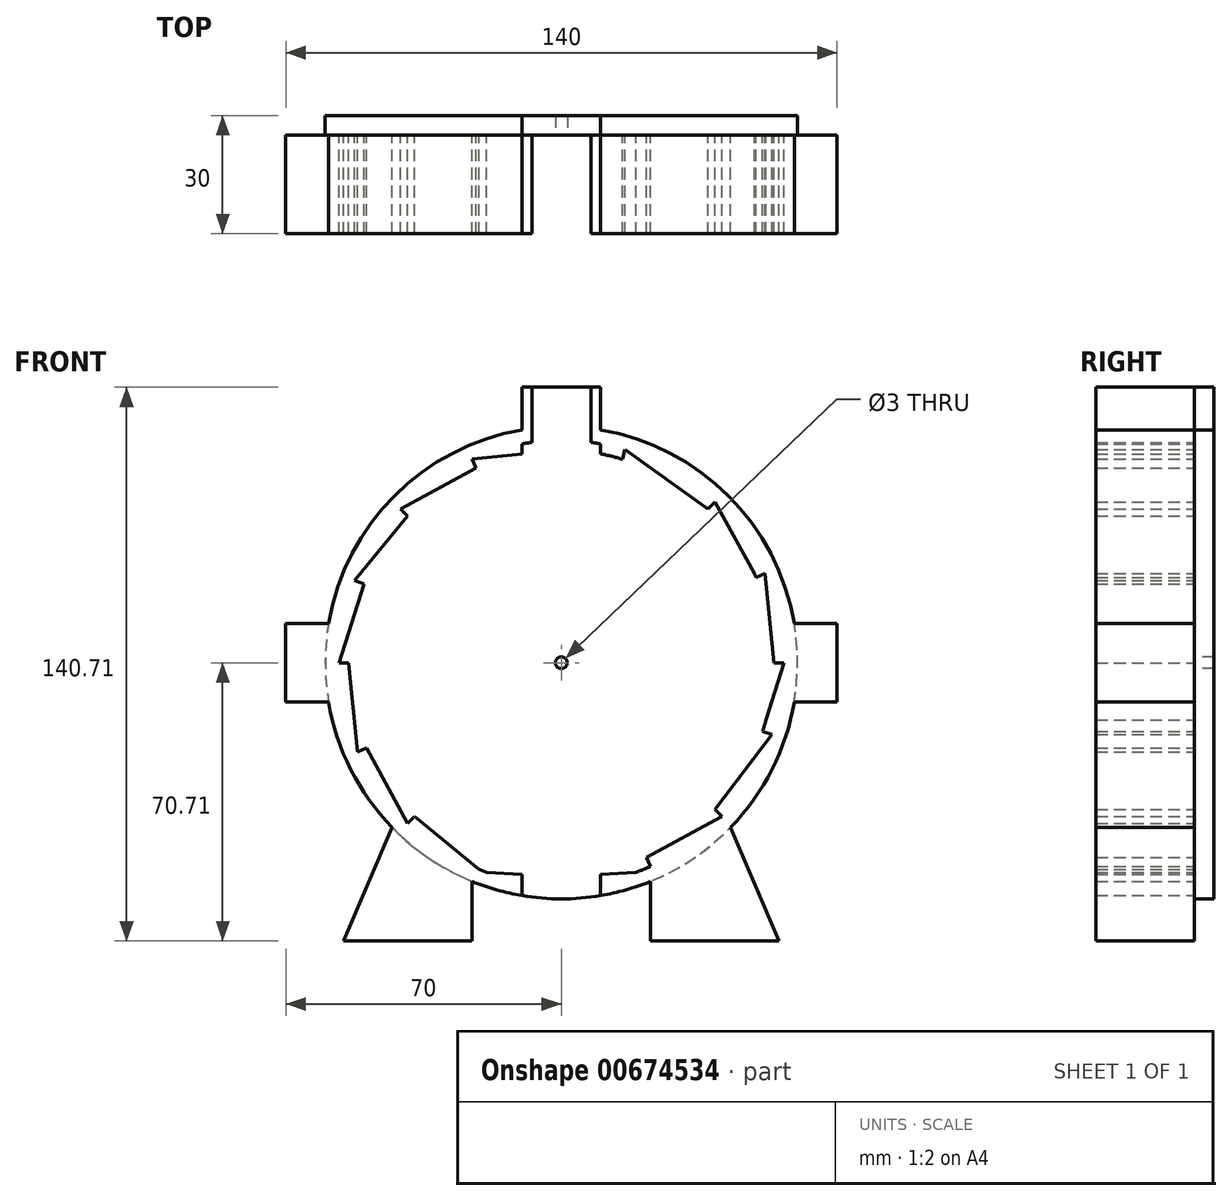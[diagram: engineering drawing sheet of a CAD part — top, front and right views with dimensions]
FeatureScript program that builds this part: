
annotation { "Feature Type Name" : "Feature", "Feature Type Description" : "" }
export const myFeature = defineFeature(function(context is Context, id is Id, definition is map)
    precondition{}
    {
        {
            var Q0;
            Q0=qCreatedBy(makeId("Front.planeOp"),FACE);
            var sketch = newSketch(context, id + "F0", { "sketchPlane" : qUnion([Q0])});
            skArc(sketch, "E0", {"start": v(-20.88, -52.5) * mm, "mid": v(-19.94, -52.87) * mm, "end": v(-18.99, -53.21) * mm});
            skArc(sketch, "E1", {"start": v(-22.63, -55.57) * mm, "mid": v(-16.42, -57.71) * mm, "end": v(-10, -59.16) * mm});
            skLineSegment(sketch, "E2", {"start": v(-10, 70) * mm, "end": v(-7.5, 70) * mm});
            skLineSegment(sketch, "E3", {"start": v(-7.5, 56) * mm, "end": v(-7.5, 70) * mm});
            skPoint(sketch, "E4.orphan", {"position": v(10, -70) * mm});
            skPoint(sketch, "E5.trimOffspring.end.orphan", {"position": v(-10, -70) * mm});
            skPoint(sketch, "E6.end.orphan", {"position": v(-17.52, -53.71) * mm});
            skPoint(sketch, "E7.orphan", {"position": v(10, -53.71) * mm});
            skPoint(sketch, "E8.MirrorCS.end.orphan", {"position": v(17.52, -53.71) * mm});
            skLineSegment(sketch, "E9", {"start": v(10, -53.71) * mm, "end": v(18.99, -53.21) * mm});
            skLineSegment(sketch, "E10.MirrorCS", {"start": v(-10, -53.71) * mm, "end": v(-18.99, -53.21) * mm});
            skLineSegment(sketch, "E11", {"start": v(56.5, 0) * mm, "end": v(54, 0) * mm});
            skLineSegment(sketch, "E12", {"start": v(54, 0) * mm, "end": v(51.77, 22.63) * mm});
            skLineSegment(sketch, "E13", {"start": v(52.02, -14.5) * mm, "end": v(56.5, 0) * mm});
            skLineSegment(sketch, "E14", {"start": v(21.63, -49.48) * mm, "end": v(40.85, -39.04) * mm});
            skLineSegment(sketch, "E15", {"start": v(39.04, -37.3) * mm, "end": v(53.49, -18.2) * mm});
            skLineSegment(sketch, "E16", {"start": v(-37.3, -39.04) * mm, "end": v(-20.88, -52.5) * mm});
            skLineSegment(sketch, "E17", {"start": v(-49.48, -21.63) * mm, "end": v(-39.04, -40.85) * mm});
            skLineSegment(sketch, "E18", {"start": v(-54, 0) * mm, "end": v(-56.5, 0) * mm});
            skLineSegment(sketch, "E19", {"start": v(-54, 0) * mm, "end": v(-51.77, -22.63) * mm});
            skLineSegment(sketch, "E20", {"start": v(-50.18, 19.96) * mm, "end": v(-56.5, 0) * mm});
            skLineSegment(sketch, "E21", {"start": v(-39.04, 37.3) * mm, "end": v(-52.5, 20.88) * mm});
            skLineSegment(sketch, "E22", {"start": v(-21.63, 49.48) * mm, "end": v(-40.85, 39.04) * mm});
            skLineSegment(sketch, "E23", {"start": v(-10, 53.07) * mm, "end": v(-22.63, 51.77) * mm});
            skLineSegment(sketch, "E24", {"start": v(49.03, 22.63) * mm, "end": v(39.04, 40.85) * mm});
            skLineSegment(sketch, "E25", {"start": v(37.3, 39.04) * mm, "end": v(16.23, 54.12) * mm});
            skLineSegment(sketch, "E26", {"start": v(22.63, -55.57) * mm, "end": v(22.63, -70.7) * mm});
            skLineSegment(sketch, "E27", {"start": v(22.63, -70.7) * mm, "end": v(55.32, -70.7) * mm});
            skLineSegment(sketch, "E28", {"start": v(55.32, -70.7) * mm, "end": v(43.02, -41.82) * mm});
            skLineSegment(sketch, "E29.MirrorCS", {"start": v(-22.63, -55.57) * mm, "end": v(-22.63, -70.7) * mm});
            skLineSegment(sketch, "E30.MirrorCS", {"start": v(-55.32, -70.7) * mm, "end": v(-43.02, -41.82) * mm});
            skLineSegment(sketch, "E31.MirrorCS", {"start": v(-22.63, -70.7) * mm, "end": v(-55.32, -70.7) * mm});
            skLineSegment(sketch, "E32", {"start": v(-70, 0) * mm, "end": v(-70, -10) * mm});
            skLineSegment(sketch, "E33.MirrorCS", {"start": v(-70, 0) * mm, "end": v(-70, 10) * mm});
            skLineSegment(sketch, "E34.MirrorCS", {"start": v(70, 0) * mm, "end": v(70, 10) * mm});
            skLineSegment(sketch, "E35.MirrorCS", {"start": v(70, 0) * mm, "end": v(70, -10) * mm});
            skLineSegment(sketch, "E36", {"start": v(70, -10) * mm, "end": v(59.16, -10) * mm});
            skLineSegment(sketch, "E37", {"start": v(70, 10) * mm, "end": v(59.16, 10) * mm});
            skLineSegment(sketch, "E38.MirrorCS", {"start": v(-70, -10) * mm, "end": v(-59.16, -10) * mm});
            skLineSegment(sketch, "E39.MirrorCS", {"start": v(-70, 10) * mm, "end": v(-59.16, 10) * mm});
            skLineSegment(sketch, "E40.trimOffspring", {"start": v(-10, -53.71) * mm, "end": v(-10, -59.16) * mm});
            skPoint(sketch, "E41.orphan", {"position": v(-22.63, -51.77) * mm});
            skLineSegment(sketch, "E42.trimOffspring", {"start": v(-37.3, -39.04) * mm, "end": v(-39.04, -40.85) * mm});
            skLineSegment(sketch, "E43.trimOffspring", {"start": v(-49.48, -21.63) * mm, "end": v(-51.77, -22.63) * mm});
            skPoint(sketch, "E44.start.orphan", {"position": v(-60, 0) * mm});
            skArc(sketch, "E45.trimOffspring", {"start": v(-59.16, -10) * mm, "mid": v(-53.51, -27.14) * mm, "end": v(-43.02, -41.82) * mm});
            skArc(sketch, "E46.trimOffspring", {"start": v(18.99, -53.21) * mm, "mid": v(20.82, -52.52) * mm, "end": v(22.63, -51.77) * mm});
            skArc(sketch, "E47.trimOffspring", {"start": v(10, -59.16) * mm, "mid": v(16.42, -57.71) * mm, "end": v(22.63, -55.57) * mm});
            skLineSegment(sketch, "E48.trimOffspring", {"start": v(10, -53.71) * mm, "end": v(10, -59.16) * mm});
            skLineSegment(sketch, "E49.trimOffspring", {"start": v(21.63, -49.48) * mm, "end": v(22.63, -51.77) * mm});
            skArc(sketch, "E50.trimOffspring", {"start": v(43.02, -41.82) * mm, "mid": v(53.51, -27.14) * mm, "end": v(59.16, -10) * mm});
            skLineSegment(sketch, "E51.trimOffspring", {"start": v(39.04, -37.3) * mm, "end": v(40.85, -39.04) * mm});
            skArc(sketch, "E52.trimOffspring", {"start": v(51.12, -17.4) * mm, "mid": v(51.6, -15.95) * mm, "end": v(52.02, -14.5) * mm});
            skLineSegment(sketch, "E53.trimOffspring", {"start": v(51.12, -17.4) * mm, "end": v(53.49, -18.2) * mm});
            skArc(sketch, "E54.trimOffspring", {"start": v(49.48, 21.63) * mm, "mid": v(49.25, 22.13) * mm, "end": v(49.03, 22.63) * mm});
            skArc(sketch, "E55.trimOffspring", {"start": v(59.16, 10) * mm, "mid": v(42.43, 42.43) * mm, "end": v(10, 59.16) * mm});
            skPoint(sketch, "E56.MirrorCS.end.orphan", {"position": v(70, 0) * mm});
            skPoint(sketch, "E56.MirrorCS.start.orphan", {"position": v(60, 0) * mm});
            skLineSegment(sketch, "E57.trimOffspring", {"start": v(49.48, 21.63) * mm, "end": v(51.77, 22.63) * mm});
            skLineSegment(sketch, "E58.trimOffspring", {"start": v(-50.18, 19.96) * mm, "end": v(-52.5, 20.88) * mm});
            skLineSegment(sketch, "E59.trimOffspring", {"start": v(-39.04, 37.3) * mm, "end": v(-40.85, 39.04) * mm});
            skLineSegment(sketch, "E60.trimOffspring", {"start": v(-21.63, 49.48) * mm, "end": v(-22.63, 51.77) * mm});
            skLineSegment(sketch, "E61.trimOffspring", {"start": v(-10, 53.07) * mm, "end": v(-10, 55.6) * mm});
            skPoint(sketch, "E62.MirrorCS.end.orphan", {"position": v(-7.5, 46.44) * mm});
            skPoint(sketch, "E62.MirrorCS.start.orphan", {"position": v(-10, 46.44) * mm});
            skLineSegment(sketch, "E63.trimOffspring", {"start": v(-10, 59.16) * mm, "end": v(-10, 70) * mm});
            skArc(sketch, "E64.trimOffspring", {"start": v(-10, 59.16) * mm, "mid": v(-42.43, 42.43) * mm, "end": v(-59.16, 10) * mm});
            skArc(sketch, "E65.trimOffspring", {"start": v(-7.5, 56) * mm, "mid": v(-8.75, 55.82) * mm, "end": v(-10, 55.6) * mm});
            skLineSegment(sketch, "E66.trimOffspring", {"start": v(7.5, 70) * mm, "end": v(10, 70) * mm});
            skLineSegment(sketch, "E67.trimOffspring", {"start": v(7.5, 56) * mm, "end": v(7.5, 70) * mm});
            skPoint(sketch, "E68.end.orphan", {"position": v(7.5, 46.44) * mm});
            skPoint(sketch, "E68.start.orphan", {"position": v(10, 46.44) * mm});
            skLineSegment(sketch, "E69.trimOffspring", {"start": v(10, 53.07) * mm, "end": v(10, 55.6) * mm});
            skLineSegment(sketch, "E70.trimOffspring", {"start": v(15.51, 51.72) * mm, "end": v(16.23, 54.12) * mm});
            skArc(sketch, "E71.trimOffspring", {"start": v(15.51, 51.72) * mm, "mid": v(12.77, 52.47) * mm, "end": v(10, 53.07) * mm});
            skLineSegment(sketch, "E72.trimOffspring", {"start": v(37.3, 39.04) * mm, "end": v(39.04, 40.85) * mm});
            skArc(sketch, "E73.trimOffspring", {"start": v(10, 55.6) * mm, "mid": v(8.75, 55.82) * mm, "end": v(7.5, 56) * mm});
            skLineSegment(sketch, "E74.trimOffspring", {"start": v(10, 59.16) * mm, "end": v(10, 70) * mm});
            skPoint(sketch, "E75.MirrorCS.start.orphan", {"position": v(-10, 0) * mm});
            skPoint(sketch, "E76.orphan", {"position": v(10, 0) * mm});
            skPoint(sketch, "E77.MirrorCS.start.orphan", {"position": v(0, -10) * mm});
            skPoint(sketch, "E78.orphan", {"position": v(0, 10) * mm});
            skPoint(sketch, "E79.start.orphan", {"position": v(-10, -10) * mm});
            skPoint(sketch, "E80.trimOffspring.end.orphan", {"position": v(10, -10) * mm});
            skPoint(sketch, "E81.end.orphan", {"position": v(10, 10) * mm});
            skPoint(sketch, "E82.trimOffspring.end.orphan", {"position": v(-10, 10) * mm});
            skPoint(sketch, "E83.trimOffspring.end.orphan", {"position": v(-10, -53.71) * mm});
            skSolve(sketch);
        }
        {
            var Q0;
            Q0 = qSketchRegion(id + "F0", true);
            extrude(context, id + "F1", {"entities" : qUnion([Q0]), "depth" : 25 * mm, "offsetDistance" : 25 * mm});
        }
        {
            var Q0;
            Q0=qCreatedBy(makeId("Front.planeOp"),FACE);
            var sketch = newSketch(context, id + "F2", { "sketchPlane" : qUnion([Q0])});
            skCircle(sketch, "E84", {"center": v(0, 0) * mm, "radius": 1.5 * mm});
            skArc(sketch, "E85", {"start": v(-10, 59.16) * mm, "mid": v(0, -60) * mm, "end": v(10, 59.16) * mm});
            skLineSegment(sketch, "E86", {"start": v(0, 70) * mm, "end": v(10, 70) * mm});
            skLineSegment(sketch, "E87.MirrorCS", {"start": v(0, 70) * mm, "end": v(-10, 70) * mm});
            skLineSegment(sketch, "E88", {"start": v(-10, 70) * mm, "end": v(-10, 59.16) * mm});
            skLineSegment(sketch, "E89", {"start": v(10, 70) * mm, "end": v(10, 59.16) * mm});
            skPoint(sketch, "E90.orphan", {"position": v(0, 60) * mm});
            skSolve(sketch);
        }
        {
            var Q0;
            Q0=makeQuery(id+"F2.imprint","IMPRINT",FACE,{"disambiguationData":[TD([[makeQuery(id+"F2.imprint","IMPRINT",EDGE,{"derivedFrom":sQuery(id+"F2.wireOp",EDGE,"E84")}),-1.0]])]});
            extrude(context, id + "F3", {"entities" : qUnion([Q0]), "oppositeDirection" : true, "depth" : 5 * mm, "offsetDistance" : 25 * mm});
        }
    });
